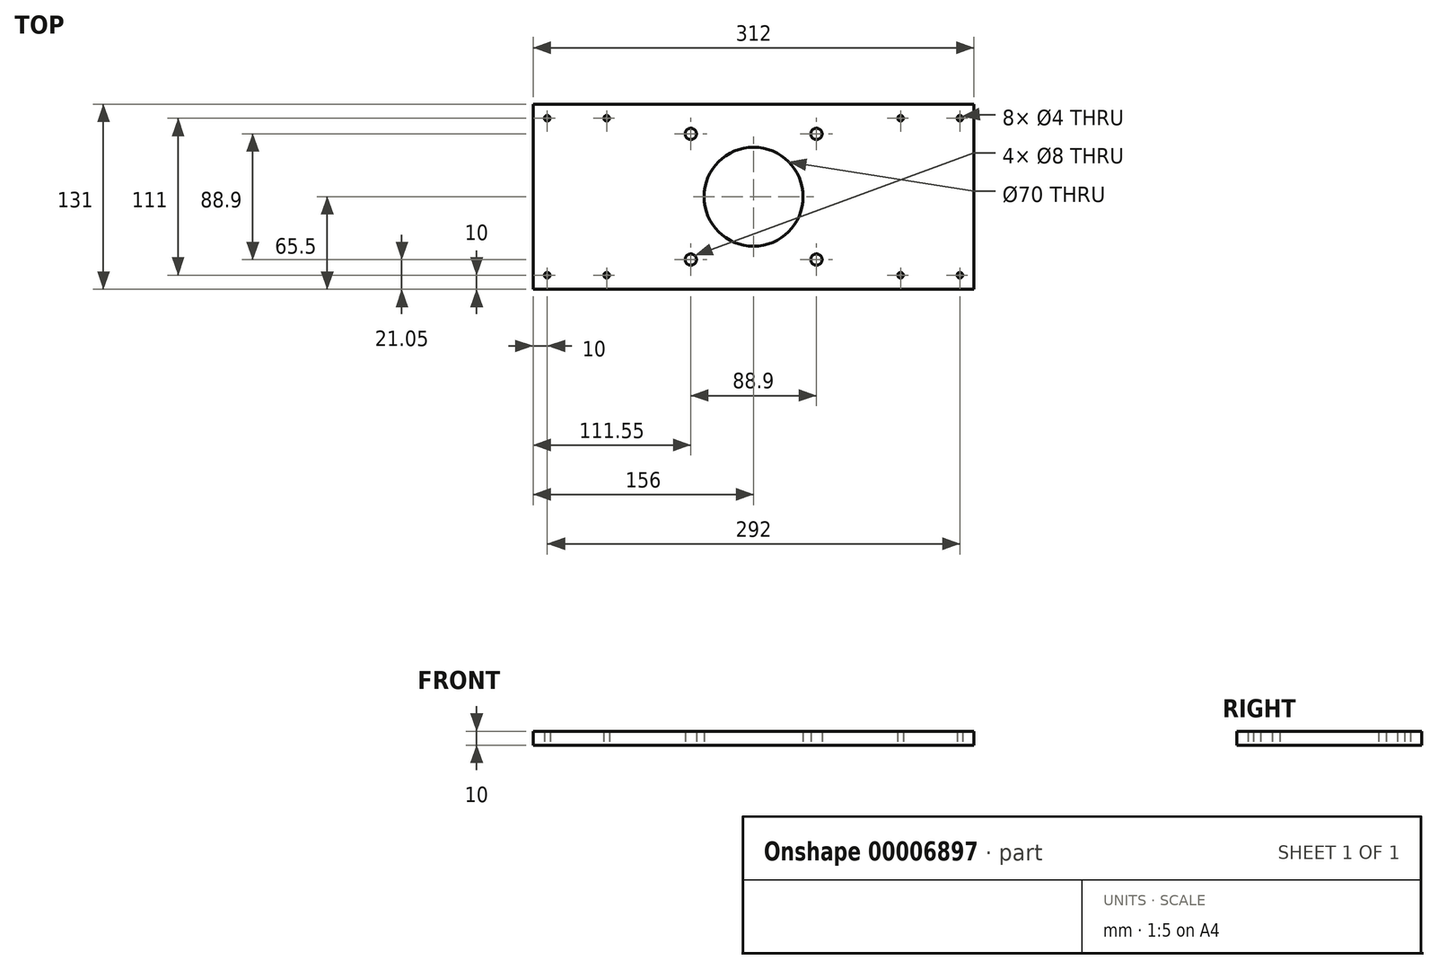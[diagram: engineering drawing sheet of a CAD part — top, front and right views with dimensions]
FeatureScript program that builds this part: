
annotation { "Feature Type Name" : "Feature", "Feature Type Description" : "" }
export const myFeature = defineFeature(function(context is Context, id is Id, definition is map)
    precondition{}
    {
        {
            var Q0;
            Q0=qCreatedBy(makeId("Top.planeOp"),FACE);
            var sketch = newSketch(context, id + "F0", { "sketchPlane" : qUnion([Q0])});
            skLineSegment(sketch, "E0.rect.bottom", {"start": v(156, -65.5) * mm, "end": v(-156, -65.5) * mm});
            skLineSegment(sketch, "E0.rect.top", {"start": v(156, 65.5) * mm, "end": v(-156, 65.5) * mm});
            skLineSegment(sketch, "E0.rect.left", {"start": v(156, -65.5) * mm, "end": v(156, 65.5) * mm});
            skLineSegment(sketch, "E0.rect.right", {"start": v(-156, -65.5) * mm, "end": v(-156, 65.5) * mm});
            skPoint(sketch, "E0.rect.middle", {"position": v(0, 0) * mm});
            skCircle(sketch, "E1", {"center": v(0, 0) * mm, "radius": 35 * mm});
            skCircle(sketch, "E2", {"center": v(-44.45, 44.45) * mm, "radius": 4 * mm});
            skCircle(sketch, "E3", {"center": v(44.45, 44.45) * mm, "radius": 4 * mm});
            skCircle(sketch, "E4", {"center": v(44.45, -44.45) * mm, "radius": 4 * mm});
            skCircle(sketch, "E5", {"center": v(-44.45, -44.45) * mm, "radius": 4 * mm});
            skCircle(sketch, "E6", {"center": v(-146, 55.5) * mm, "radius": 2 * mm});
            skCircle(sketch, "E7", {"center": v(-104, 55.5) * mm, "radius": 2 * mm});
            skCircle(sketch, "E8", {"center": v(-146, -55.5) * mm, "radius": 2 * mm});
            skCircle(sketch, "E9", {"center": v(-104, -55.5) * mm, "radius": 2 * mm});
            skCircle(sketch, "E10", {"center": v(146, -55.5) * mm, "radius": 2 * mm});
            skCircle(sketch, "E11", {"center": v(104, -55.5) * mm, "radius": 2 * mm});
            skCircle(sketch, "E12", {"center": v(146, 55.5) * mm, "radius": 2 * mm});
            skCircle(sketch, "E13", {"center": v(104, 55.5) * mm, "radius": 2 * mm});
            skLineSegment(sketch, "E14", {"start": v(-113, 0) * mm, "end": v(185, 0) * mm, "construction": true});
            skLineSegment(sketch, "E15", {"start": v(0, 88.94) * mm, "end": v(0, -137.61) * mm, "construction": true});
            skSolve(sketch);
        }
        {
            var Q0;
            Q0=qSketchRegion(id+"F0",true);
            var Q1;
            Q1=makeQuery(id+"F0.imprint","IMPRINT",FACE,{"disambiguationData":[TD([[makeQuery(id+"F0.imprint","IMPRINT",EDGE,{"derivedFrom":sQuery(id+"F0.wireOp",EDGE,"E0.rect.bottom")}),-1.0]])]});
            extrude(context, id + "F1", {"entities" : qUnion([Q0, Q1]), "depth" : 10 * mm});
        }
    });
